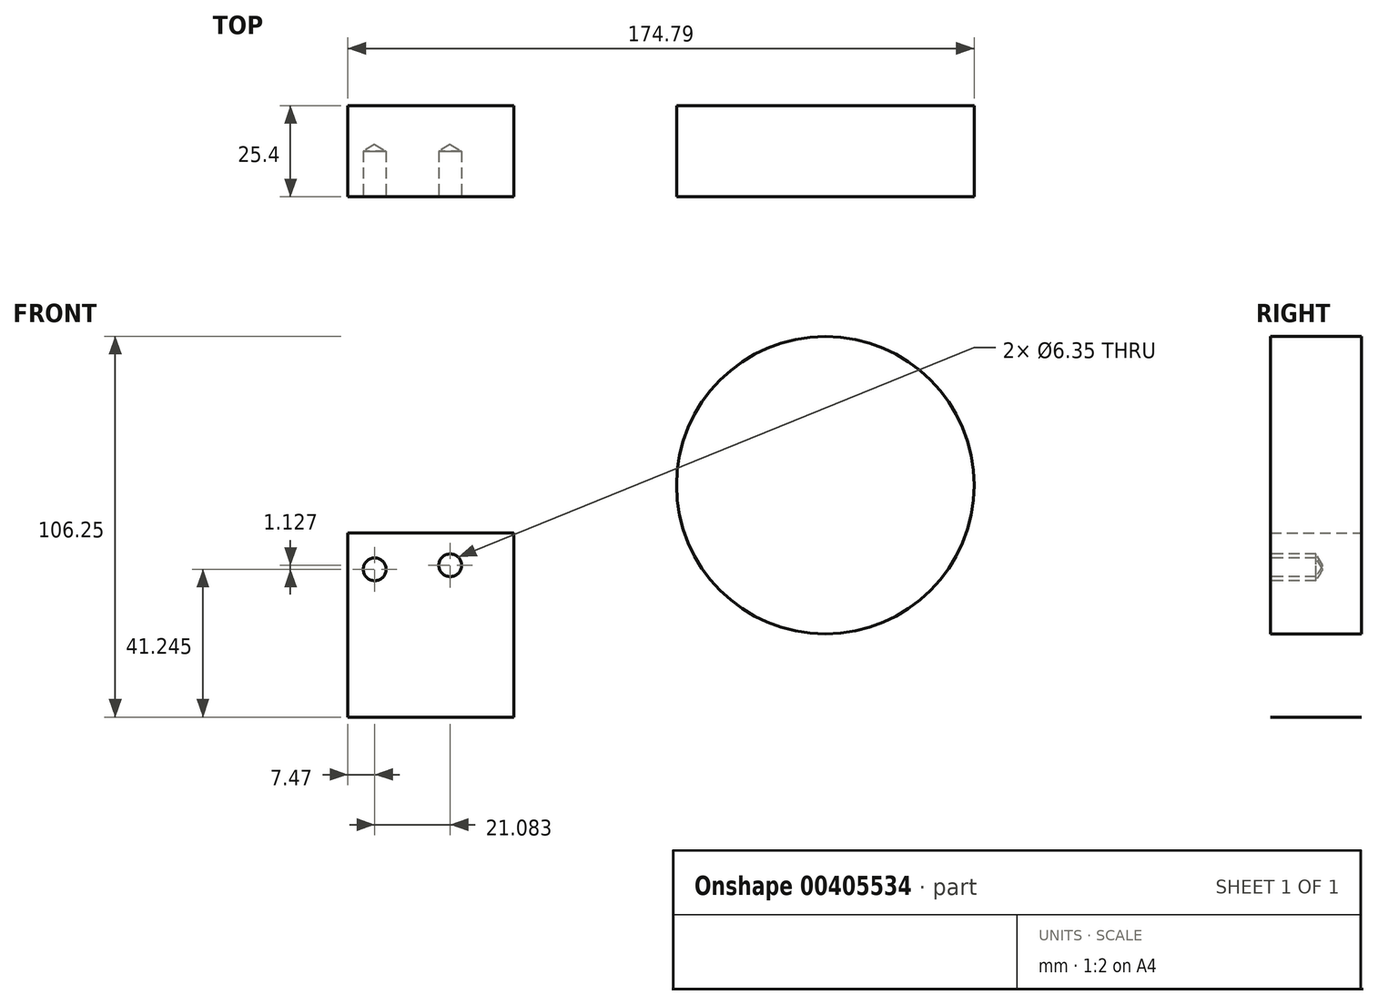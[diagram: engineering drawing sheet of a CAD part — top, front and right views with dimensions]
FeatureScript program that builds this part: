
annotation { "Feature Type Name" : "Feature", "Feature Type Description" : "" }
export const myFeature = defineFeature(function(context is Context, id is Id, definition is map)
    precondition{}
    {
        {
            var Q0;
            Q0=qCreatedBy(makeId("Front.planeOp"),FACE);
            var sketch = newSketch(context, id + "F0", { "sketchPlane" : qUnion([Q0])});
            skLineSegment(sketch, "E0.bottom", {"start": v(-64.7, 37.98) * mm, "end": v(-18.44, 37.98) * mm});
            skLineSegment(sketch, "E0.top", {"start": v(-64.7, -13.46) * mm, "end": v(-18.44, -13.46) * mm});
            skLineSegment(sketch, "E0.left", {"start": v(-64.7, 37.98) * mm, "end": v(-64.7, -13.46) * mm});
            skLineSegment(sketch, "E0.right", {"start": v(-18.44, 37.98) * mm, "end": v(-18.44, -13.46) * mm});
            skSolve(sketch);
        }
        {
            var Q0;
            Q0 = qSketchRegion(id + "F0", true);
            extrude(context, id + "F1", {"entities" : qUnion([Q0]), "depth" : 25.4 * mm});
        }
        {
            var Q0;
            Q0=makeQuery(id+"F1.opExtrude","CAP_FACE",FACE,{"disambiguationData":[OSD([sQuery(id+"F0.wireOp",EDGE,"E0.bottom"),sQuery(id+"F0.wireOp",EDGE,"E0.top"),sQuery(id+"F0.wireOp",EDGE,"E0.left"),sQuery(id+"F0.wireOp",EDGE,"E0.right")])],"isStart":false});
            var sketch = newSketch(context, id + "F2", { "sketchPlane" : qUnion([Q0])});
            skPoint(sketch, "E1", {"position": v(-57.24, 27.78) * mm});
            skPoint(sketch, "E2", {"position": v(-36.16, 28.91) * mm});
            skSolve(sketch);
        }
        {
            var Q0;
            Q0=sQuery(id+"F2.wireOp",VERTEX,"E1");
            var Q1;
            Q1=sQuery(id+"F2.wireOp",VERTEX,"E2");
            var Q2;
            Q2=makeQuery(id+"F1.opExtrude","SWEPT_BODY",BODY,{"disambiguationData":[OSD([sQuery(id+"F0.wireOp",EDGE,"E0.bottom"),sQuery(id+"F0.wireOp",EDGE,"E0.top"),sQuery(id+"F0.wireOp",EDGE,"E0.left"),sQuery(id+"F0.wireOp",EDGE,"E0.right")])]});
            hole(context, id + "F3", {"style" : HoleStyle.SIMPLE, "endStyle" : HoleEndStyle.BLIND, "holeDiameter" : 6.35 * mm, "holeDepth" : 12.7 * mm, "isTappedThrough" : true, "tappedDepth" : 12.7 * mm, "tapClearance" : 3, "locations" : qUnion([Q0, Q1]), "scope" : qUnion([Q2])});
        }
        {
            var Q0;
            Q0=qCreatedBy(makeId("Front.planeOp"),FACE);
            var sketch = newSketch(context, id + "F4", { "sketchPlane" : qUnion([Q0])});
            skCircle(sketch, "E3", {"center": v(68.54, 51.26) * mm, "radius": 41.54 * mm});
            skSolve(sketch);
        }
        {
            var Q0;
            Q0 = qSketchRegion(id + "F4", true);
            extrude(context, id + "F5", {"entities" : qUnion([Q0]), "depth" : 25.4 * mm});
        }
    });
